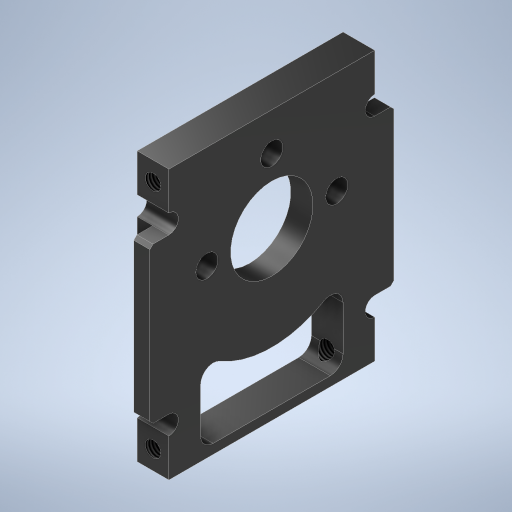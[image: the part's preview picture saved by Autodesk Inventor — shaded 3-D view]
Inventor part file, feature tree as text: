
AUTODESK INVENTOR PART (.ipt)
format: ipt  version: 2024.2 (Build 282272000, 272)  size: 398,848 bytes
history: native  units: mm
features: hole x4, extrude x3, sketch x2, fillet x2, chamfer x1, mirror x1
ambient origin geometry x8: Origin, YZ Plane, XZ Plane, XY Plane, X Axis, Y Axis, Z Axis, Center Point
bodies: Solid1 (feature_tree)
feature tree (13):
  sketch  "Sketch1"  dims[d0=1.5mm d1=32.5mm]
  extrude  "Extrusion1"  Depth=32.5mm
  extrude  "Extrusion2"  Depth=9.0mm
  extrude  "Extrusion3"  Depth=3.0mm
  chamfer  "Chamfer1"  Distance=40.0mm Angle=360.0deg
  fillet  "Fillet1"  Radius=20.5mm
  fillet  "Fillet2"  Radius=29.5mm
  sketch  "Sketch2"  dims[d2=42.5mm d4=9.0mm d5=3.0mm d6=40.0mm d8=360.0deg d10=20.5mm d11=29.5mm d12=25.0mm d13=0.05mm d14=40.0mm d16=360.0deg d19=1.45mm d20=6.0mm d21=1.5mm d22=5.0mm d23=5.0mm d24=0.0mm d25=1.5mm d26=0.0mm d27=2.45mm d28=0.0mm d29=13.0mm d30=6.0mm d31=4.0mm d32=2.0mm d33=90.0deg d34=8.0mm d35=20.594885mm d36=3.5mm d37=6.0mm d38=4.0mm d39=2.0mm d40=90.0deg d41=8.0mm d42=20.594885mm d43=0.5mm d44=2.0mm d45=45.0deg d46=2.0mm d47=2.459mm d48=6.0mm d49=4.0mm d50=2.0mm d51=90.0deg d52=6.0mm d53=0.0mm d54=2.459mm d55=6.0mm d56=4.0mm d57=2.0mm d58=90.0deg d59=6.0mm d60=0.0mm d61=2.0mm]
  hole  "Hole1"  [1 undecoded]
  hole  "Hole2"  [1 undecoded]
  hole  "Hole3"  [1 undecoded]
  hole  "Hole4"  [1 undecoded]
  mirror  "Mirror1"
note: 4 required parameter values undecoded (feature->parameter linkage not recoverable at this tier; creation-order binding heuristic only, values carry confidence <= 0.55)
